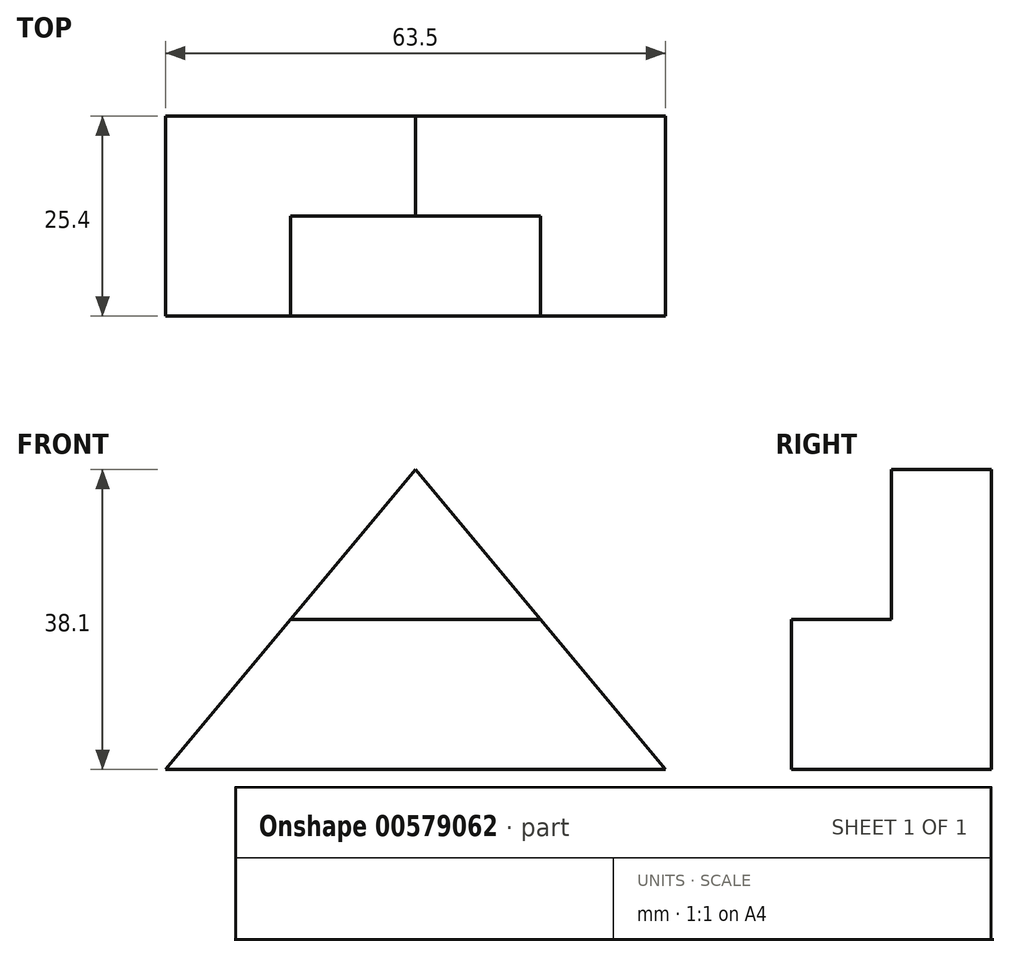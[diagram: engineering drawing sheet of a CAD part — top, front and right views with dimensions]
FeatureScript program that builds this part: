
annotation { "Feature Type Name" : "Feature", "Feature Type Description" : "" }
export const myFeature = defineFeature(function(context is Context, id is Id, definition is map)
    precondition{}
    {
        {
            var Q0;
            Q0=qCreatedBy(makeId("Front.planeOp"),FACE);
            var sketch = newSketch(context, id + "F0", { "sketchPlane" : qUnion([Q0])});
            skLineSegment(sketch, "E0.top", {"start": v(0, 0) * mm, "end": v(63.5, 0) * mm});
            skLineSegment(sketch, "E1", {"start": v(0, 19.05) * mm, "end": v(0, 19.05) * mm});
            skLineSegment(sketch, "E2", {"start": v(15.88, 19.05) * mm, "end": v(47.62, 19.05) * mm});
            skLineSegment(sketch, "E3", {"start": v(0, 0) * mm, "end": v(15.88, 19.05) * mm});
            skLineSegment(sketch, "E4", {"start": v(31.75, 38.1) * mm, "end": v(47.62, 19.05) * mm});
            skLineSegment(sketch, "E5", {"start": v(15.88, 19.05) * mm, "end": v(31.75, 38.1) * mm});
            skLineSegment(sketch, "E6", {"start": v(47.62, 19.05) * mm, "end": v(63.5, 0) * mm});
            skPoint(sketch, "E7.orphan", {"position": v(0, 38.1) * mm});
            skPoint(sketch, "E0.right.start.orphan", {"position": v(63.5, 38.1) * mm});
            skSolve(sketch);
        }
        {
            var Q0;
            Q0=makeQuery(id+"F0.imprint","IMPRINT",FACE,{"disambiguationData":[TD([[makeQuery(id+"F0.imprint","IMPRINT",EDGE,{"derivedFrom":sQuery(id+"F0.wireOp",EDGE,"E0.top")}),1.0]])]});
            extrude(context, id + "F1", {"entities" : qUnion([Q0]), "depth" : 25.4 * mm, "offsetDistance" : 25.4 * mm});
        }
        {
            var Q0;
            Q0 = qSketchRegion(id + "F0", true);
            extrude(context, id + "F2", {"entities" : qUnion([Q0]), "operationType" : NewBodyOperationType.ADD, "depth" : 12.7 * mm, "offsetDistance" : 25.4 * mm});
        }
    });
